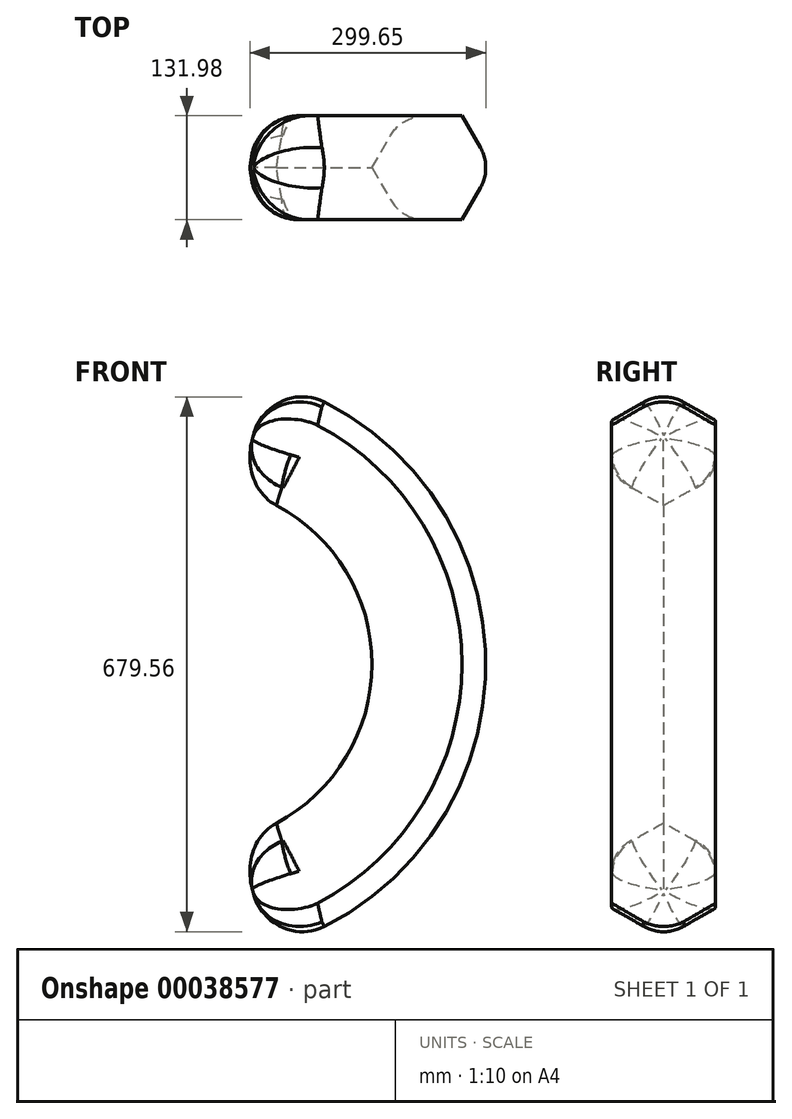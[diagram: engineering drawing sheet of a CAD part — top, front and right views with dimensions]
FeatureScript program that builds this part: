
annotation { "Feature Type Name" : "Feature", "Feature Type Description" : "" }
export const myFeature = defineFeature(function(context is Context, id is Id, definition is map)
    precondition{}
    {
        {
            var Q0;
            Q0=qCreatedBy(makeId("Top.planeOp"),FACE);
            var sketch = newSketch(context, id + "F0", { "sketchPlane" : qUnion([Q0])});
            skCircle(sketch, "E0.cCircle", {"center": v(0, 0) * mm, "radius": 76.2 * mm, "construction": true});
            skLineSegment(sketch, "E0.0", {"start": v(-76.2, 0) * mm, "end": v(-38.1, 66) * mm});
            skLineSegment(sketch, "E0.1", {"start": v(-38.1, 66) * mm, "end": v(38.1, 66) * mm});
            skLineSegment(sketch, "E0.2", {"start": v(38.1, 66) * mm, "end": v(76.2, 0) * mm});
            skLineSegment(sketch, "E0.3", {"start": v(76.2, 0) * mm, "end": v(38.1, -66) * mm});
            skLineSegment(sketch, "E0.4", {"start": v(38.1, -66) * mm, "end": v(-38.1, -66) * mm});
            skLineSegment(sketch, "E0.5", {"start": v(-38.1, -66) * mm, "end": v(-76.2, 0) * mm});
            skLineSegment(sketch, "E1", {"start": v(-304.8, 68.55) * mm, "end": v(-304.8, -66.59) * mm});
            skSolve(sketch);
        }
        {
            var Q0;
            Q0=makeQuery(id+"F0.imprint","IMPRINT",FACE,{"disambiguationData":[TD([[makeQuery(id+"F0.imprint","IMPRINT",EDGE,{"derivedFrom":sQuery(id+"F0.wireOp",EDGE,"E0.0")}),-1.0]])]});
            var Q1;
            Q1=sQuery(id+"F0.wireOp",EDGE,"E1");
            revolve(context, id + "F1", {"entities" : qUnion([Q0]), "axis" : qUnion([Q1]), "revolveType" : RevolveType.SYMMETRIC, "angle" : 150 * degree});
        }
        {
            var Q0;
            Q0=makeQuery(id+"F1.opRevolve","SWEPT_EDGE",EDGE,{"disambiguationData":[OSD([sQuery(id+"F0.wireOp",EDGE,"E0.2"),sQuery(id+"F0.wireOp",EDGE,"E0.3")])]});
            var Q1;
            Q1=makeQuery(id+"F1.opRevolve","SWEPT_EDGE",EDGE,{"disambiguationData":[OSD([sQuery(id+"F0.wireOp",EDGE,"E0.4"),sQuery(id+"F0.wireOp",EDGE,"E0.5")])]});
            var Q2;
            Q2=makeQuery(id+"F1.opRevolve","SWEPT_EDGE",EDGE,{"disambiguationData":[OSD([sQuery(id+"F0.wireOp",EDGE,"E0.0"),sQuery(id+"F0.wireOp",EDGE,"E0.1")])]});
            fillet(context, id + "F2", {"entities" : qUnion([Q0, Q1, Q2]), "radius" : 50.8 * mm, "tangentPropagation" : true, "allowEdgeOverflow" : false});
        }
        {
            var Q0;
            Q0=makeQuery(id+"F1.opRevolve","CAP_FACE",FACE,{"disambiguationData":[OSD([sQuery(id+"F0.wireOp",EDGE,"E0.0"),sQuery(id+"F0.wireOp",EDGE,"E0.1"),sQuery(id+"F0.wireOp",EDGE,"E0.2"),sQuery(id+"F0.wireOp",EDGE,"E0.3"),sQuery(id+"F0.wireOp",EDGE,"E0.4"),sQuery(id+"F0.wireOp",EDGE,"E0.5")])],"isStart":false});
            var Q1;
            Q1=makeQuery(id+"F1.opRevolve","CAP_FACE",FACE,{"disambiguationData":[OSD([sQuery(id+"F0.wireOp",EDGE,"E0.0"),sQuery(id+"F0.wireOp",EDGE,"E0.1"),sQuery(id+"F0.wireOp",EDGE,"E0.2"),sQuery(id+"F0.wireOp",EDGE,"E0.3"),sQuery(id+"F0.wireOp",EDGE,"E0.4"),sQuery(id+"F0.wireOp",EDGE,"E0.5")])],"isStart":true});
            fillet(context, id + "F3", {"entities" : qUnion([Q0, Q1]), "radius" : 63.5 * mm, "tangentPropagation" : true, "allowEdgeOverflow" : false});
        }
    });
